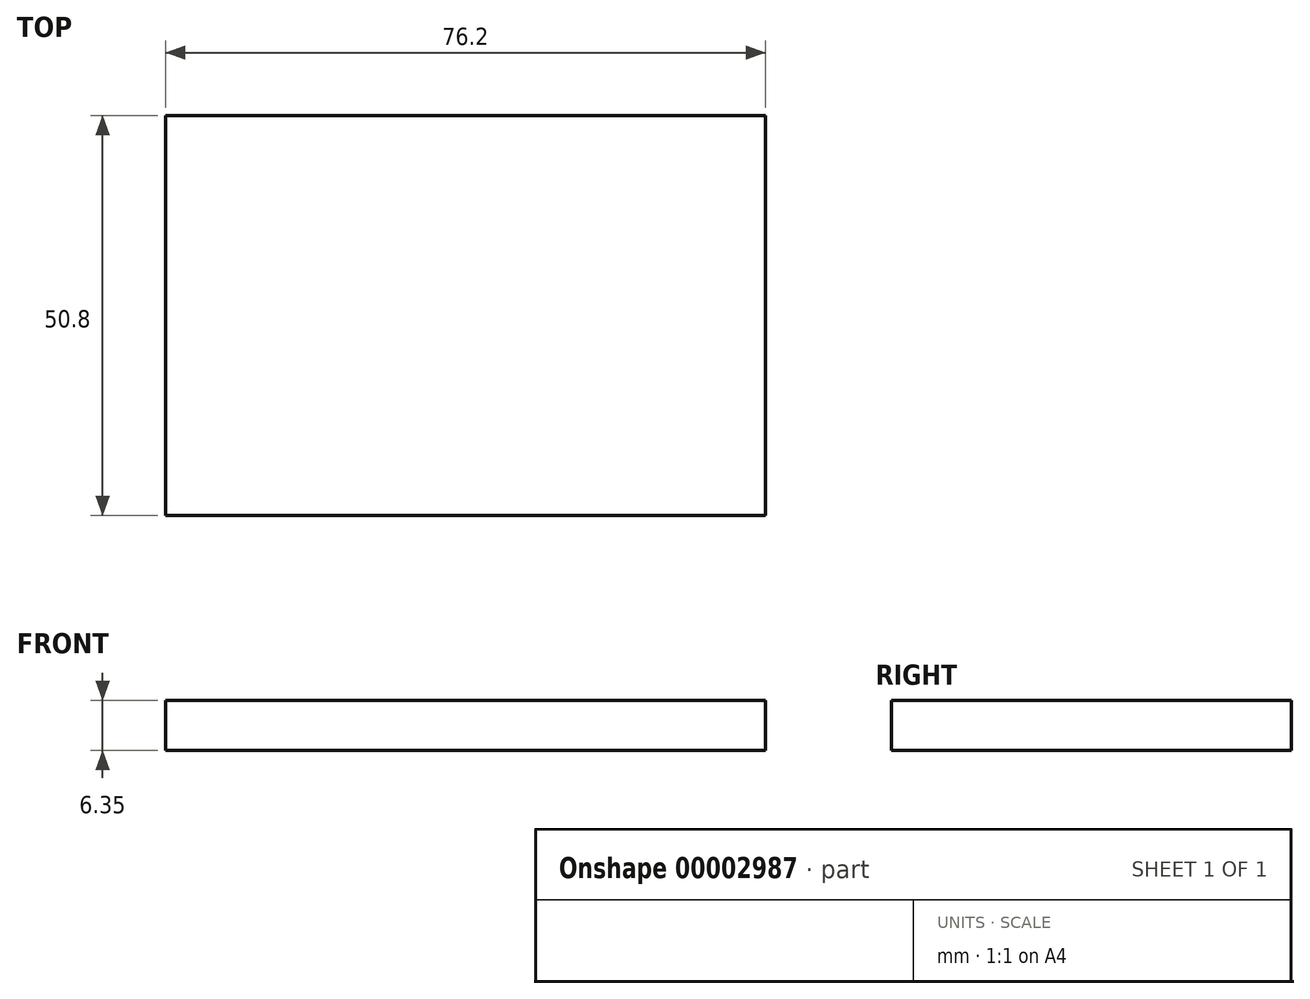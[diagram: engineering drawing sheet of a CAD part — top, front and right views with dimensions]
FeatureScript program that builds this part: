
annotation { "Feature Type Name" : "Feature", "Feature Type Description" : "" }
export const myFeature = defineFeature(function(context is Context, id is Id, definition is map)
    precondition{}
    {
        {
            var Q0;
            Q0=qCreatedBy(makeId("Top.planeOp"),FACE);
            var sketch = newSketch(context, id + "F0", { "sketchPlane" : qUnion([Q0])});
            skLineSegment(sketch, "E0.bottom", {"start": v(-38.1, 25.4) * mm, "end": v(38.1, 25.4) * mm});
            skLineSegment(sketch, "E0.top", {"start": v(-38.1, -25.4) * mm, "end": v(38.1, -25.4) * mm});
            skLineSegment(sketch, "E0.left", {"start": v(-38.1, 25.4) * mm, "end": v(-38.1, -25.4) * mm});
            skLineSegment(sketch, "E0.right", {"start": v(38.1, 25.4) * mm, "end": v(38.1, -25.4) * mm});
            skLineSegment(sketch, "E1", {"start": v(0, 25.4) * mm, "end": v(0, 0) * mm, "construction": true});
            skLineSegment(sketch, "E2", {"start": v(0, 0) * mm, "end": v(38.1, 0) * mm, "construction": true});
            skSolve(sketch);
        }
        {
            var Q0;
            Q0=makeQuery(id+"F0.imprint","IMPRINT",FACE,{"disambiguationData":[TD([[makeQuery(id+"F0.imprint","IMPRINT",EDGE,{"derivedFrom":sQuery(id+"F0.wireOp",EDGE,"E0.bottom")}),-1.0]])]});
            extrude(context, id + "F1", {"entities" : qUnion([Q0]), "depth" : 6.35 * mm});
        }
        {
            var Q0;
            Q0=qCreatedBy(makeId("Top.planeOp"),FACE);
            var sketch = newSketch(context, id + "F2", { "sketchPlane" : qUnion([Q0])});
            skArc(sketch, "E3", {"start": v(3.84, 11.9) * mm, "mid": v(-10.46, 2.26) * mm, "end": v(-19.05, -12.7) * mm});
            skArc(sketch, "E4", {"start": v(13.8, 7) * mm, "mid": v(-5.28, 1.58) * mm, "end": v(-19.05, -12.7) * mm});
            skSolve(sketch);
        }
        {
            var Q0;
            Q0=makeQuery(id+"F1.opExtrude","SWEPT_FACE",FACE,{"disambiguationData":[OSD([sQuery(id+"F0.wireOp",EDGE,"E0.top")])]});
            var sketch = newSketch(context, id + "F3", { "sketchPlane" : qUnion([Q0])});
            skLineSegment(sketch, "E5", {"start": v(-19.05, 5.35) * mm, "end": v(3.84, 4.35) * mm});
            skLineSegment(sketch, "E6", {"start": v(-19.05, 5.35) * mm, "end": v(13.8, 4.35) * mm});
            skSolve(sketch);
        }
        {
            var Q0;
            Q0=sQuery(id+"F2.wireOp",EDGE,"E3");
            var Q1;
            Q1=makeQuery(id+"F1.opExtrude","CAP_FACE",FACE,{"disambiguationData":[OSD([sQuery(id+"F0.wireOp",EDGE,"E0.bottom"),sQuery(id+"F0.wireOp",EDGE,"E0.top"),sQuery(id+"F0.wireOp",EDGE,"E0.left"),sQuery(id+"F0.wireOp",EDGE,"E0.right")])],"isStart":false});
            extrude(context, id + "F4", {"bodyType" : ToolBodyType.SURFACE, "surfaceEntities" : qUnion([Q0]), "endBound" : BoundingType.UP_TO_SURFACE, "endBoundEntityFace" : qUnion([Q1]), "depth" : 25.4 * mm});
        }
        {
            var Q0;
            Q0=sQuery(id+"F2.wireOp",EDGE,"E4");
            var Q1;
            Q1=makeQuery(id+"F1.opExtrude","CAP_FACE",FACE,{"disambiguationData":[OSD([sQuery(id+"F0.wireOp",EDGE,"E0.bottom"),sQuery(id+"F0.wireOp",EDGE,"E0.top"),sQuery(id+"F0.wireOp",EDGE,"E0.left"),sQuery(id+"F0.wireOp",EDGE,"E0.right")])],"isStart":false});
            extrude(context, id + "F5", {"bodyType" : ToolBodyType.SURFACE, "surfaceEntities" : qUnion([Q0]), "endBound" : BoundingType.UP_TO_SURFACE, "endBoundEntityFace" : qUnion([Q1]), "depth" : 25.4 * mm});
        }
        {
            var Q0;
            Q0=sQuery(id+"F3.wireOp",EDGE,"E5");
            var Q1;
            Q1=makeQuery(id+"F1.opExtrude","SWEPT_FACE",FACE,{"disambiguationData":[OSD([sQuery(id+"F0.wireOp",EDGE,"E0.bottom")])]});
            extrude(context, id + "F6", {"bodyType" : ToolBodyType.SURFACE, "surfaceEntities" : qUnion([Q0]), "endBound" : BoundingType.UP_TO_SURFACE, "oppositeDirection" : true, "endBoundEntityFace" : qUnion([Q1]), "depth" : 25.4 * mm});
        }
        {
            var Q0;
            Q0=sQuery(id+"F3.wireOp",EDGE,"E6");
            var Q1;
            Q1=makeQuery(id+"F1.opExtrude","SWEPT_FACE",FACE,{"disambiguationData":[OSD([sQuery(id+"F0.wireOp",EDGE,"E0.bottom")])]});
            extrude(context, id + "F7", {"bodyType" : ToolBodyType.SURFACE, "surfaceEntities" : qUnion([Q0]), "endBound" : BoundingType.UP_TO_SURFACE, "oppositeDirection" : true, "endBoundEntityFace" : qUnion([Q1]), "depth" : 25.4 * mm});
        }
    });
